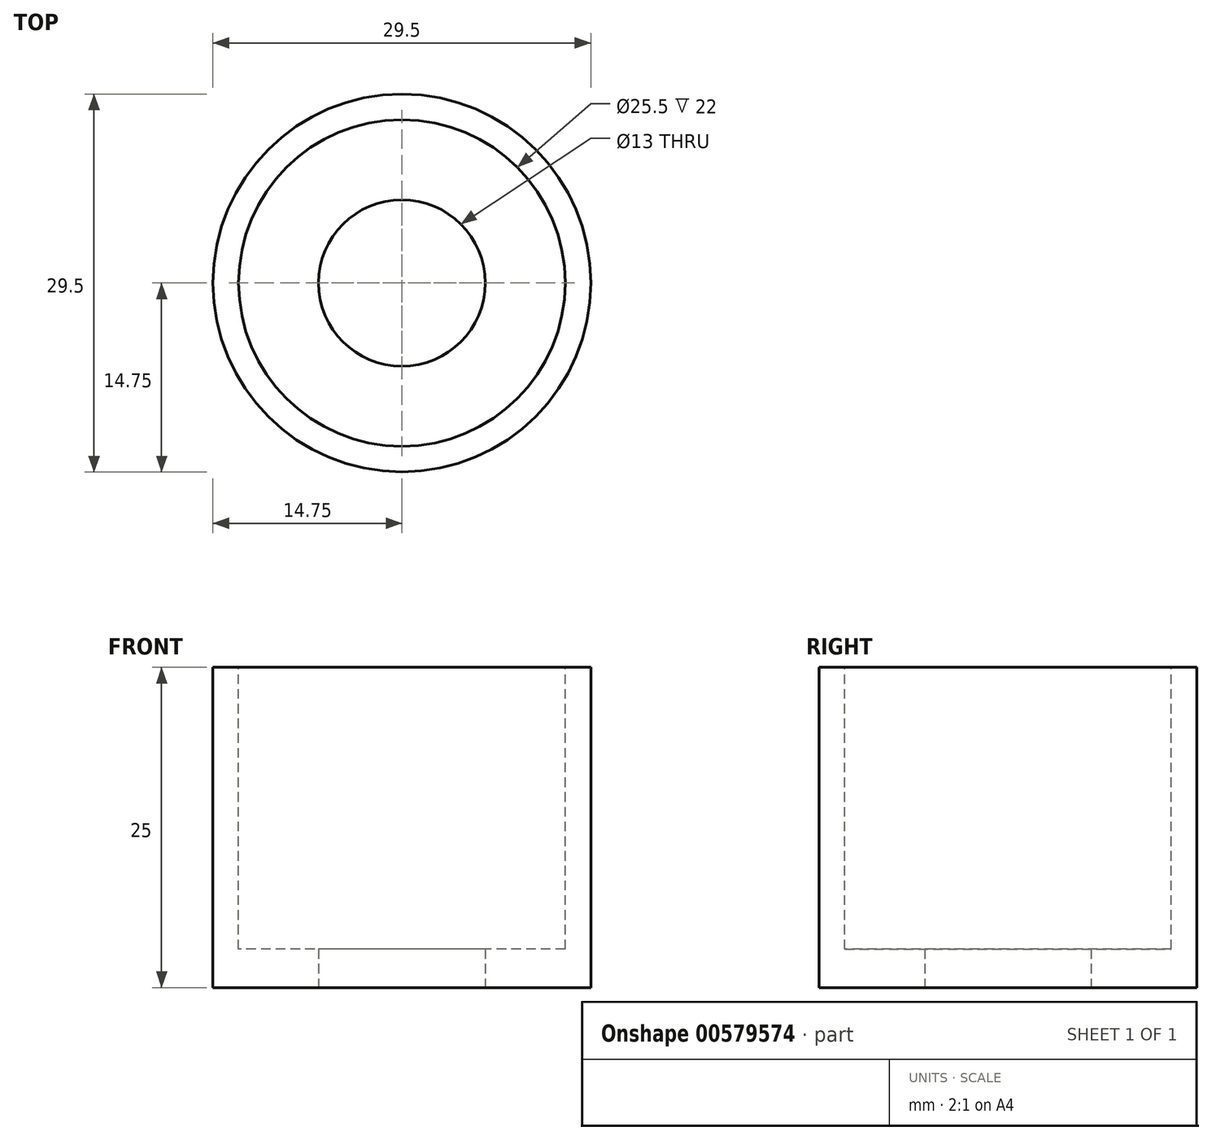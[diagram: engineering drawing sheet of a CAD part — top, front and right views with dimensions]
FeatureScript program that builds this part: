
annotation { "Feature Type Name" : "Feature", "Feature Type Description" : "" }
export const myFeature = defineFeature(function(context is Context, id is Id, definition is map)
    precondition{}
    {
        {
            var Q0;
            Q0=qCreatedBy(makeId("Top.planeOp"),FACE);
            var sketch = newSketch(context, id + "F0", { "sketchPlane" : qUnion([Q0])});
            skCircle(sketch, "E0", {"center": v(0, 0) * mm, "radius": 14.75 * mm});
            skSolve(sketch);
        }
        {
            var Q0;
            Q0=makeQuery(id+"F0.imprint","IMPRINT",FACE,{"disambiguationData":[TD([[makeQuery(id+"F0.imprint","IMPRINT",EDGE,{"derivedFrom":sQuery(id+"F0.wireOp",EDGE,"E0")}),1.0]])]});
            extrude(context, id + "F1", {"entities" : qUnion([Q0]), "depth" : 25 * mm, "offsetDistance" : 25 * mm});
        }
        {
            var Q0;
            Q0=makeQuery(id+"F1.opExtrude","CAP_FACE",FACE,{"disambiguationData":[OSD([sQuery(id+"F0.wireOp",EDGE,"E0")])],"isStart":false});
            var sketch = newSketch(context, id + "F2", { "sketchPlane" : qUnion([Q0])});
            skCircle(sketch, "E1", {"center": v(0, 0) * mm, "radius": 12.75 * mm});
            skSolve(sketch);
        }
        {
            var Q0;
            Q0=makeQuery(id+"F2.imprint","IMPRINT",FACE,{"disambiguationData":[TD([[makeQuery(id+"F2.imprint","IMPRINT",EDGE,{"derivedFrom":sQuery(id+"F2.wireOp",EDGE,"E1")}),1.0]])]});
            extrude(context, id + "F3", {"entities" : qUnion([Q0]), "operationType" : NewBodyOperationType.REMOVE, "oppositeDirection" : true, "depth" : 22 * mm, "offsetDistance" : 25 * mm});
        }
        {
            var Q0;
            Q0=makeQuery(id+"F1.opExtrude","CAP_FACE",FACE,{"disambiguationData":[OSD([sQuery(id+"F0.wireOp",EDGE,"E0")])],"isStart":true});
            var sketch = newSketch(context, id + "F4", { "sketchPlane" : qUnion([Q0])});
            skCircle(sketch, "E2", {"center": v(0, 0) * mm, "radius": 6.5 * mm});
            skSolve(sketch);
        }
        {
            var Q0;
            Q0=makeQuery(id+"F4.imprint","IMPRINT",FACE,{"disambiguationData":[TD([[makeQuery(id+"F4.imprint","IMPRINT",EDGE,{"derivedFrom":sQuery(id+"F4.wireOp",EDGE,"E2")}),1.0]])]});
            extrude(context, id + "F5", {"entities" : qUnion([Q0]), "operationType" : NewBodyOperationType.REMOVE, "oppositeDirection" : true, "depth" : 25 * mm, "offsetDistance" : 25 * mm});
        }
    });
